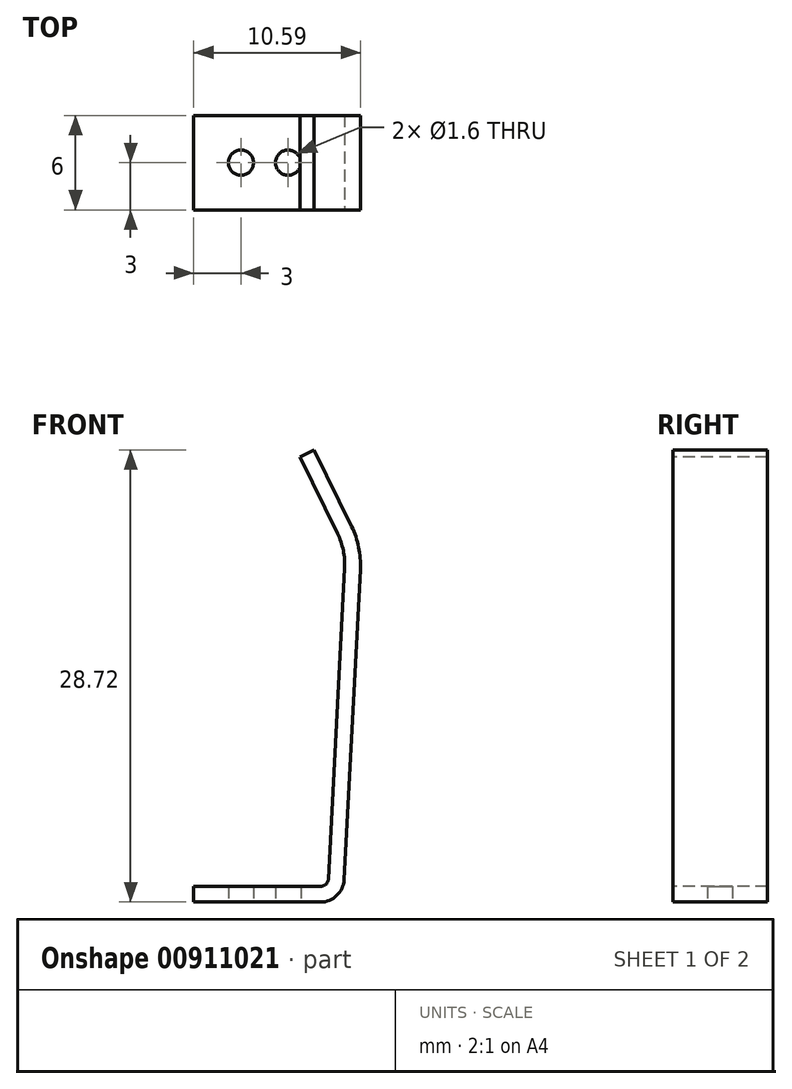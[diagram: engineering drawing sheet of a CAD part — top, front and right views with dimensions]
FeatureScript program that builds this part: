
annotation { "Feature Type Name" : "Feature", "Feature Type Description" : "" }
export const myFeature = defineFeature(function(context is Context, id is Id, definition is map)
    precondition{}
    {
        {
            var Q0;
            Q0=qCreatedBy(makeId("Right.planeOp"),FACE);
            var sketch = newSketch(context, id + "F0", { "sketchPlane" : qUnion([Q0])});
            skLineSegment(sketch, "E0.bottom", {"start": v(3, -0.5) * mm, "end": v(-3, -0.5) * mm});
            skLineSegment(sketch, "E0.top", {"start": v(3, 0.5) * mm, "end": v(-3, 0.5) * mm});
            skLineSegment(sketch, "E0.left", {"start": v(3, -0.5) * mm, "end": v(3, 0.5) * mm});
            skLineSegment(sketch, "E0.right", {"start": v(-3, -0.5) * mm, "end": v(-3, 0.5) * mm});
            skPoint(sketch, "E0.middle", {"position": v(0, 0) * mm});
            skSolve(sketch);
        }
        {
            var Q0;
            Q0=qCreatedBy(makeId("Front.planeOp"),FACE);
            var sketch = newSketch(context, id + "F1", { "sketchPlane" : qUnion([Q0])});
            skLineSegment(sketch, "E1", {"start": v(0, 0) * mm, "end": v(8.05, 0) * mm});
            skLineSegment(sketch, "E2", {"start": v(9.05, 0.95) * mm, "end": v(10.08, 20.67) * mm});
            skLineSegment(sketch, "E3", {"start": v(9.58, 23.14) * mm, "end": v(7.19, 28) * mm});
            skPoint(sketch, "E4.visualSharp", {"position": v(10.15, 21.97) * mm});
            skArc(sketch, "E4.filletArc", {"start": v(10.08, 20.67) * mm, "mid": v(9.99, 21.94) * mm, "end": v(9.58, 23.14) * mm});
            skPoint(sketch, "E5.visualSharp", {"position": v(9, 0) * mm});
            skArc(sketch, "E5.filletArc", {"start": v(8.05, 0) * mm, "mid": v(8.74, 0.27) * mm, "end": v(9.05, 0.95) * mm});
            skSolve(sketch);
        }
        {
            var Q0;
            Q0=makeQuery(id+"F0.imprint","IMPRINT",FACE,{"disambiguationData":[TD([[makeQuery(id+"F0.imprint","IMPRINT",EDGE,{"derivedFrom":sQuery(id+"F0.wireOp",EDGE,"E0.bottom")}),-1.0]])]});
            var Q1;
            Q1=sQuery(id+"F1.wireOp",EDGE,"E1");
            var Q2;
            Q2=sQuery(id+"F1.wireOp",EDGE,"E5.filletArc");
            var Q3;
            Q3=sQuery(id+"F1.wireOp",EDGE,"E2");
            var Q4;
            Q4=sQuery(id+"F1.wireOp",EDGE,"E4.filletArc");
            var Q5;
            Q5=sQuery(id+"F1.wireOp",EDGE,"E3");
            sweep(context, id + "F2", {"profiles" : qUnion([Q0]), "path" : qUnion([Q1, Q2, Q3, Q4, Q5])});
        }
        {
            var Q0;
            Q0=makeQuery(id+"F2.opSweep","SWEPT_FACE",FACE,{"disambiguationData":[OSD([sQuery(id+"F0.wireOp",EDGE,"E0.top"),sQuery(id+"F1.wireOp",EDGE,"E1")])]});
            var sketch = newSketch(context, id + "F3", { "sketchPlane" : qUnion([Q0])});
            skLineSegment(sketch, "E6", {"start": v(0, 0) * mm, "end": v(3, 0) * mm, "construction": true});
            skLineSegment(sketch, "E7", {"start": v(3, 0) * mm, "end": v(6, 0) * mm, "construction": true});
            skCircle(sketch, "E8", {"center": v(3, 0) * mm, "radius": 0.8 * mm});
            skCircle(sketch, "E9", {"center": v(6, 0) * mm, "radius": 0.8 * mm});
            skSolve(sketch);
        }
        {
            var Q0;
            Q0=makeQuery(id+"F3.imprint","IMPRINT",FACE,{"disambiguationData":[TD([[makeQuery(id+"F3.imprint","IMPRINT",EDGE,{"derivedFrom":sQuery(id+"F3.wireOp",EDGE,"E8")}),1.0]])]});
            var Q1;
            Q1=makeQuery(id+"F3.imprint","IMPRINT",FACE,{"disambiguationData":[TD([[makeQuery(id+"F3.imprint","IMPRINT",EDGE,{"derivedFrom":sQuery(id+"F3.wireOp",EDGE,"E9")}),1.0]])]});
            extrude(context, id + "F4", {"entities" : qUnion([Q0, Q1]), "operationType" : NewBodyOperationType.REMOVE, "endBound" : BoundingType.SYMMETRIC, "depth" : 2 * mm, "offsetDistance" : 25 * mm});
        }
    });
